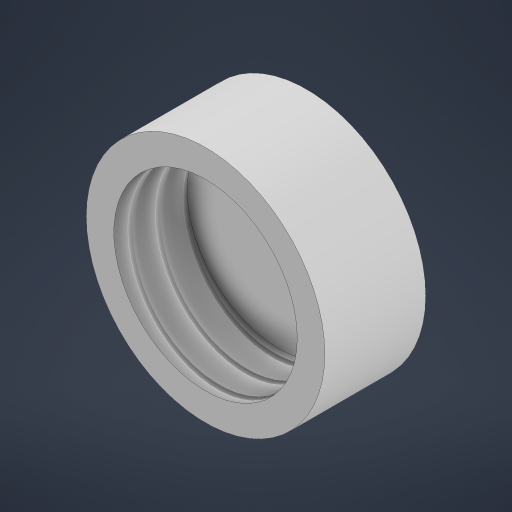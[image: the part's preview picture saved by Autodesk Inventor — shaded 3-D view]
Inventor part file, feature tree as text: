
AUTODESK INVENTOR PART (.ipt)
format: ipt  version: 2023 (Build 270158000, 158)  size: 198,656 bytes
history: native  units: mm
features: sketch x2, extrude x1, hole x1, thread x1
ambient origin geometry x8: Origin, YZ Plane, XZ Plane, XY Plane, X Axis, Y Axis, Z Axis, Center Point
bodies: Solid1 (feature_tree)
feature tree (5):
  extrude  "Extrusion1"  Depth=5.5mm TaperAngle=0.0deg
  hole  "Hole1"  [1 undecoded]
  thread  "Thread1"  [1 undecoded]
  sketch  "Sketch1"  dims[d0=13.0mm d1=5.5mm d2=0.0mm]
  sketch  "Sketch2"  dims[d3=10.0mm d4=6.0mm d5=4.0mm d6=2.0mm d7=90.0deg d8=4.0mm d9=0.0mm d10=4.0mm d11=0.0mm]
note: 2 required parameter values undecoded (feature->parameter linkage not recoverable at this tier; creation-order binding heuristic only, values carry confidence <= 0.55)
